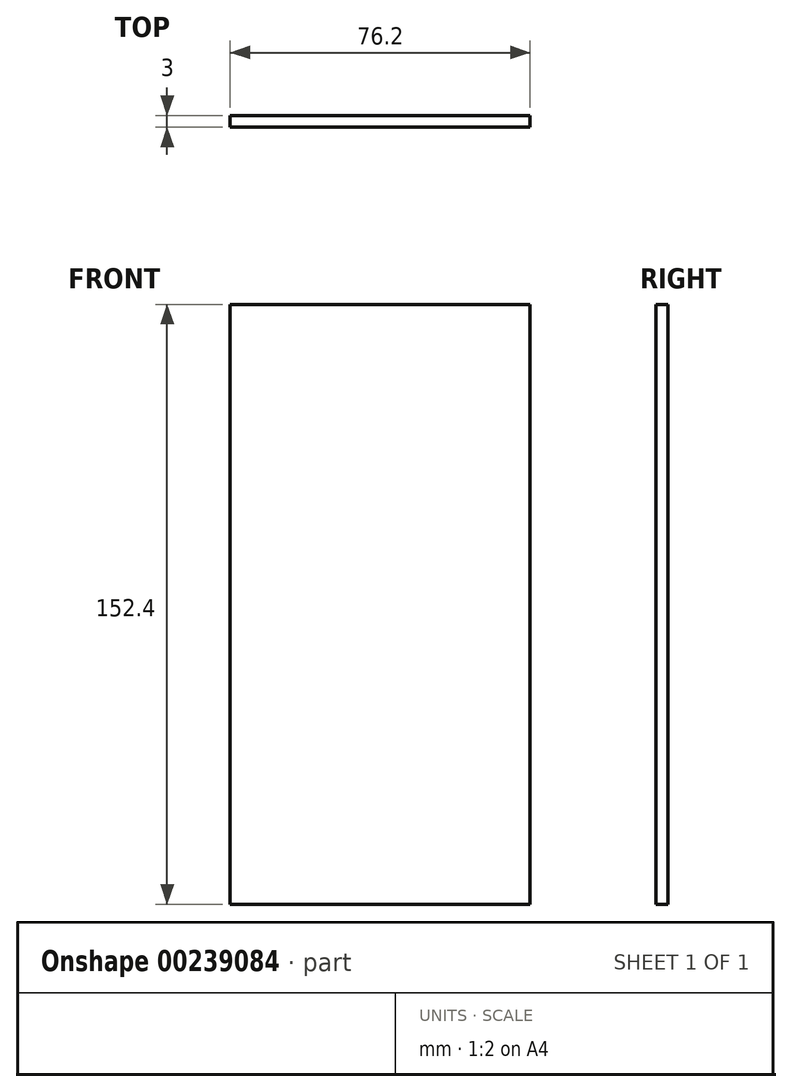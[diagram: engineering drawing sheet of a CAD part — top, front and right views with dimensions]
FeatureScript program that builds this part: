
annotation { "Feature Type Name" : "Feature", "Feature Type Description" : "" }
export const myFeature = defineFeature(function(context is Context, id is Id, definition is map)
    precondition{}
    {
        {
            assignVariable(context, id + "F0", {"name" : "v", "anyValue" : 3});
        }
        {
            var Q0;
            Q0=qCreatedBy(makeId("Front.planeOp"),FACE);
            var sketch = newSketch(context, id + "F1", { "sketchPlane" : qUnion([Q0])});
            skLineSegment(sketch, "E0.bottom", {"start": v(-38.1, 76.2) * mm, "end": v(38.1, 76.2) * mm});
            skLineSegment(sketch, "E0.top", {"start": v(-38.1, -76.2) * mm, "end": v(38.1, -76.2) * mm});
            skLineSegment(sketch, "E0.left", {"start": v(-38.1, 76.2) * mm, "end": v(-38.1, -76.2) * mm});
            skLineSegment(sketch, "E0.right", {"start": v(38.1, 76.2) * mm, "end": v(38.1, -76.2) * mm});
            skPoint(sketch, "E0.middle", {"position": v(0, 0) * mm});
            skSolve(sketch);
        }
        {
            var Q0;
            Q0 = qSketchRegion(id + "F1", true);
            extrude(context, id + "F2", {"entities" : qUnion([Q0]), "endBound" : BoundingType.SYMMETRIC, "depth" : (getVariable(context, 'v')) * mm});
        }
    });
